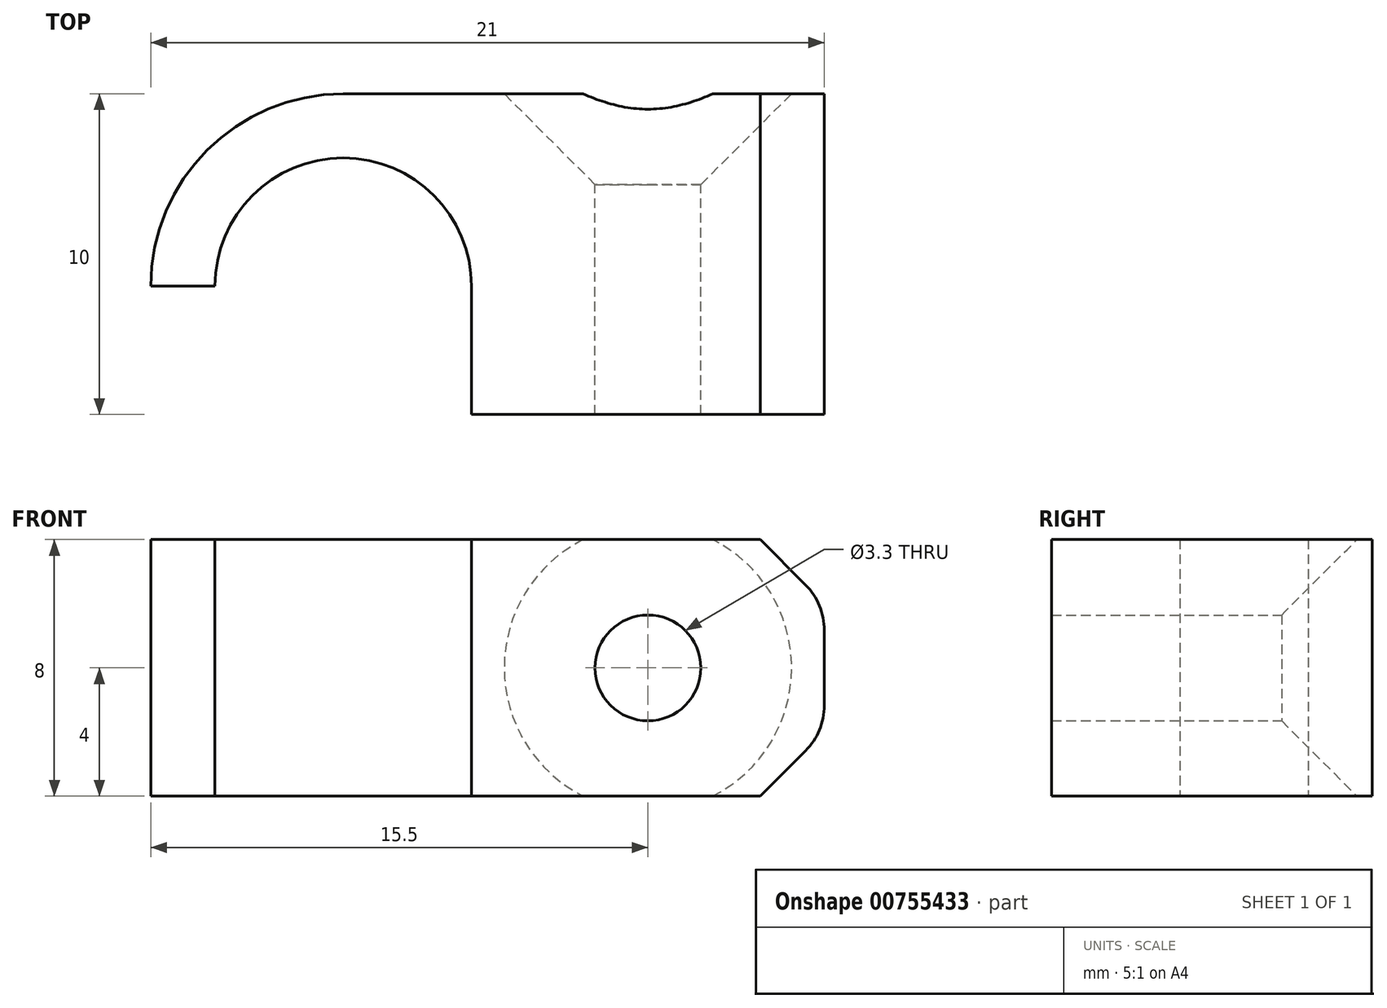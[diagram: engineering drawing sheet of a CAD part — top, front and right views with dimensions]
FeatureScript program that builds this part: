
annotation { "Feature Type Name" : "Feature", "Feature Type Description" : "" }
export const myFeature = defineFeature(function(context is Context, id is Id, definition is map)
    precondition{}
    {
        {
            var Q0;
            Q0=qCreatedBy(makeId("Top.planeOp"),FACE);
            var sketch = newSketch(context, id + "F0", { "sketchPlane" : qUnion([Q0])});
            skArc(sketch, "E0", {"start": v(4, 0) * mm, "mid": v(0, 4) * mm, "end": v(-4, 0) * mm});
            skArc(sketch, "E1.0", {"start": v(0, 6) * mm, "mid": v(-4.24, 4.24) * mm, "end": v(-6, 0) * mm});
            skLineSegment(sketch, "E2", {"start": v(0, 6) * mm, "end": v(15, 6) * mm});
            skLineSegment(sketch, "E3", {"start": v(15, 6) * mm, "end": v(15, -4) * mm});
            skLineSegment(sketch, "E4", {"start": v(4, -4) * mm, "end": v(15, -4) * mm});
            skLineSegment(sketch, "E5", {"start": v(-6, 0) * mm, "end": v(-4, 0) * mm});
            skLineSegment(sketch, "E6", {"start": v(4, 0) * mm, "end": v(4, -4) * mm});
            skPoint(sketch, "E7.orphan", {"position": v(0, -4) * mm});
            skSolve(sketch);
        }
        {
            var Q0;
            Q0=makeQuery(id+"F0.imprint","IMPRINT",FACE,{"disambiguationData":[TD([[makeQuery(id+"F0.imprint","IMPRINT",EDGE,{"derivedFrom":sQuery(id+"F0.wireOp",EDGE,"E0")}),-1.0]])]});
            extrude(context, id + "F1", {"entities" : qUnion([Q0]), "endBound" : BoundingType.SYMMETRIC, "depth" : 8 * mm, "offsetDistance" : 25 * mm});
        }
        {
            var Q0;
            Q0=makeQuery(id+"F1.opExtrude","SWEPT_FACE",FACE,{"disambiguationData":[OSD([sQuery(id+"F0.wireOp",EDGE,"E2")])]});
            var sketch = newSketch(context, id + "F2", { "sketchPlane" : qUnion([Q0])});
            skLineSegment(sketch, "E8", {"start": v(-15, 4) * mm, "end": v(-4, -4) * mm, "construction": true});
            skPoint(sketch, "E9", {"position": v(-9.5, 0) * mm});
            skSolve(sketch);
        }
        {
            var Q0;
            Q0=sQuery(id+"F2.wireOp",VERTEX,"E9");
            var Q1;
            Q1=makeQuery(id+"F1.opExtrude","SWEPT_BODY",BODY,{"disambiguationData":[OSD([sQuery(id+"F0.wireOp",EDGE,"E0"),sQuery(id+"F0.wireOp",EDGE,"E1.0"),sQuery(id+"F0.wireOp",EDGE,"E2"),sQuery(id+"F0.wireOp",EDGE,"E3"),sQuery(id+"F0.wireOp",EDGE,"E4"),sQuery(id+"F0.wireOp",EDGE,"E5"),sQuery(id+"F0.wireOp",EDGE,"E6")])]});
            hole(context, id + "F3", {"style" : HoleStyle.C_SINK, "endStyle" : HoleEndStyle.THROUGH, "standardTappedOrClearance" : lookupTablePath({ "standard" : "ISO", "engagement" : "75%", "pitch" : "0.7 mm", "size" : "M4", "type" : "Tapped" }), "standardBlindInLast" : lookupTablePath({ "standard" : "ISO", "engagement" : "75%", "pitch" : "0.7 mm", "size" : "M4", "type" : "Tapped" }), "holeDiameter" : 3.3 * mm, "cSinkDiameter" : 8.96 * mm, "cSinkAngle" : 90 * degree, "majorDiameter" : 4 * mm, "showTappedDepth" : true, "isTappedThrough" : true, "tappedDepth" : 12 * mm, "tapClearance" : 3, "locations" : qUnion([Q0]), "scope" : qUnion([Q1])});
        }
        {
            var Q0;
            Q0=makeQuery(id+"F1.opExtrude","CAP_EDGE",EDGE,{"disambiguationData":[OSD([sQuery(id+"F0.wireOp",EDGE,"E3")])],"isStart":true});
            var Q1;
            Q1=makeQuery(id+"F1.opExtrude","CAP_EDGE",EDGE,{"disambiguationData":[OSD([sQuery(id+"F0.wireOp",EDGE,"E3")])],"isStart":false});
            chamfer(context, id + "F4", {"entities" : qUnion([Q0, Q1]), "width" : 2 * mm, "tangentPropagation" : true});
        }
        {
            var Q0;
            {var subQ0=sQuery(id+"F0.wireOp",EDGE,"E3");Q0=makeQuery(id+"F4.opChamfer","BLEND_EDGE",EDGE,{"blendedFrom":[makeQuery(id+"F1.opExtrude","CAP_EDGE",EDGE,{"disambiguationData":[OSD([subQ0])],"isStart":false}),makeQuery(id+"F1.opExtrude","SWEPT_FACE",FACE,{"disambiguationData":[OSD([subQ0])]})],"blendedInto":[makeQuery(id+"F1.opExtrude","SWEPT_FACE",FACE,{"disambiguationData":[OSD([subQ0])]})]});}
            var Q1;
            {var subQ0=sQuery(id+"F0.wireOp",EDGE,"E3");Q1=makeQuery(id+"F4.opChamfer","BLEND_EDGE",EDGE,{"blendedFrom":[makeQuery(id+"F1.opExtrude","CAP_EDGE",EDGE,{"disambiguationData":[OSD([subQ0])],"isStart":true}),makeQuery(id+"F1.opExtrude","SWEPT_FACE",FACE,{"disambiguationData":[OSD([subQ0])]})],"blendedInto":[makeQuery(id+"F1.opExtrude","SWEPT_FACE",FACE,{"disambiguationData":[OSD([subQ0])]})]});}
            fillet(context, id + "F5", {"entities" : qUnion([Q0, Q1]), "radius" : 2 * mm, "tangentPropagation" : true, "allowEdgeOverflow" : false});
        }
    });
